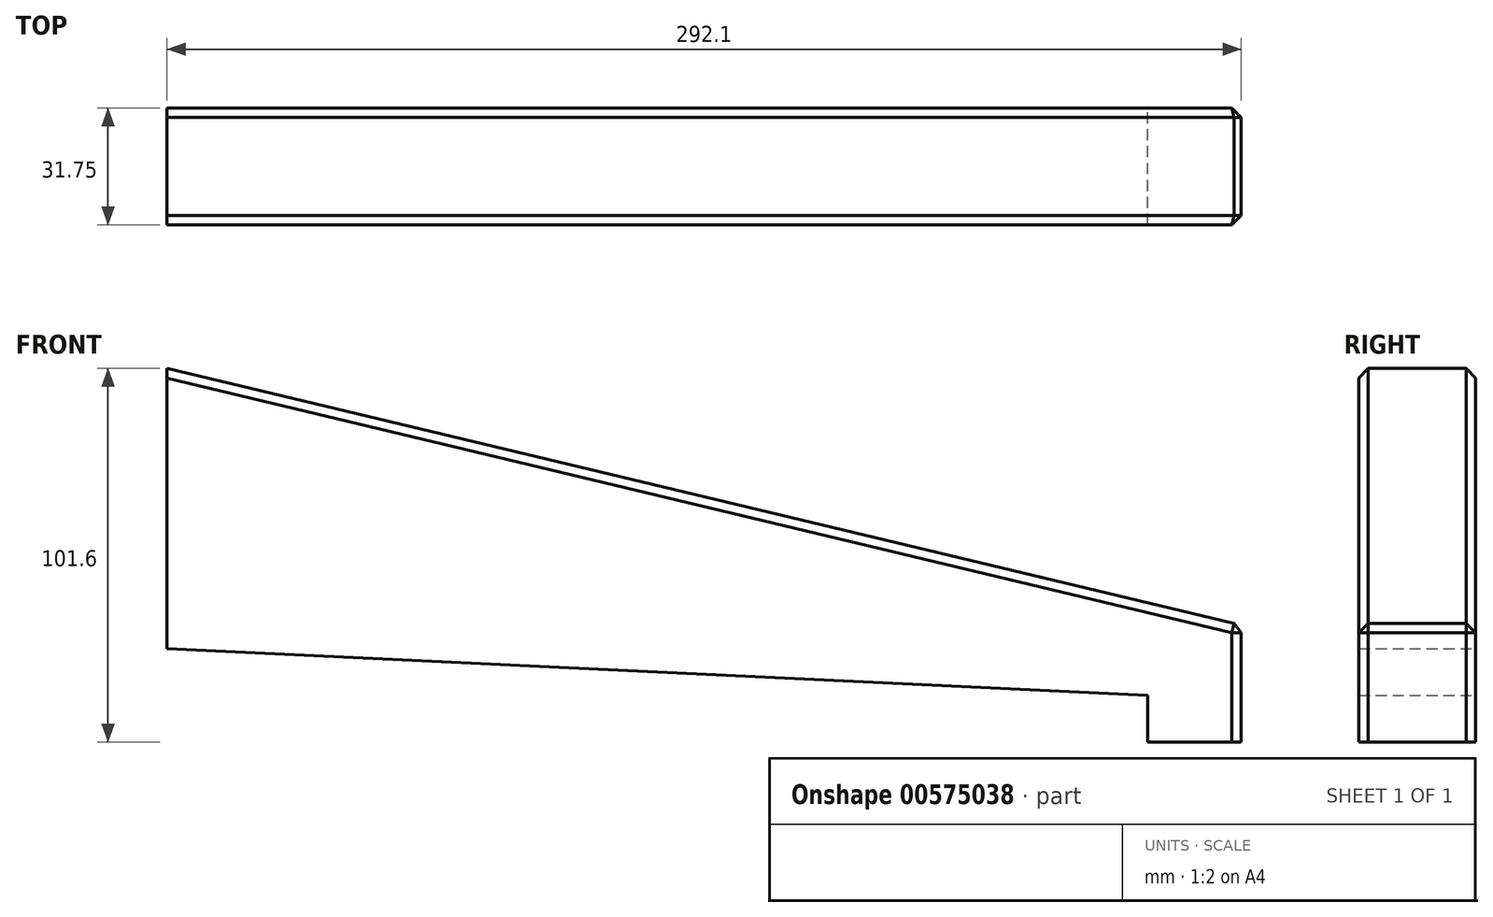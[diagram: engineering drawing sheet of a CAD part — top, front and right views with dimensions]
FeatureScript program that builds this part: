
annotation { "Feature Type Name" : "Feature", "Feature Type Description" : "" }
export const myFeature = defineFeature(function(context is Context, id is Id, definition is map)
    precondition{}
    {
        {
            var Q0;
            Q0=qCreatedBy(makeId("Front.planeOp"),FACE);
            var sketch = newSketch(context, id + "F0", { "sketchPlane" : qUnion([Q0])});
            skLineSegment(sketch, "E0.right", {"start": v(146.05, 6.35) * mm, "end": v(146.05, -12.7) * mm});
            skPoint(sketch, "E0.middle", {"position": v(0, 0) * mm});
            skLineSegment(sketch, "E1", {"start": v(146.05, -12.7) * mm, "end": v(120.65, -12.7) * mm});
            skLineSegment(sketch, "E2", {"start": v(120.65, -12.7) * mm, "end": v(120.65, 0) * mm});
            skLineSegment(sketch, "E3", {"start": v(120.65, 0) * mm, "end": v(-146.05, 12.7) * mm});
            skLineSegment(sketch, "E4", {"start": v(-146.05, 12.7) * mm, "end": v(-146.05, 88.9) * mm});
            skLineSegment(sketch, "E5", {"start": v(146.05, 6.35) * mm, "end": v(146.05, 19.05) * mm});
            skLineSegment(sketch, "E6", {"start": v(-146.05, 88.9) * mm, "end": v(146.05, 19.05) * mm});
            skLineSegment(sketch, "E7", {"start": v(120.65, 0) * mm, "end": v(-146.05, 0) * mm});
            skSolve(sketch);
        }
        {
            var Q0;
            Q0=makeQuery(id+"F0.imprint","IMPRINT",FACE,{"disambiguationData":[TD([[makeQuery(id+"F0.imprint","IMPRINT",EDGE,{"derivedFrom":sQuery(id+"F0.wireOp",EDGE,"E0.right")}),-1.0]])]});
            extrude(context, id + "F1", {"entities" : qUnion([Q0]), "depth" : 31.75 * mm, "offsetDistance" : 25.4 * mm});
        }
        {
            var Q0;
            Q0=makeQuery(id+"F1.opExtrude","CAP_EDGE",EDGE,{"disambiguationData":[OSD([sQuery(id+"F0.wireOp",EDGE,"E6")])],"isStart":false});
            var Q1;
            Q1=makeQuery(id+"F1.opExtrude","CAP_EDGE",EDGE,{"disambiguationData":[OSD([sQuery(id+"F0.wireOp",EDGE,"E6")])],"isStart":true});
            var Q2;
            Q2=makeQuery(id+"F1.opExtrude","SWEPT_EDGE",EDGE,{"disambiguationData":[OSD([sQuery(id+"F0.wireOp",EDGE,"E5"),sQuery(id+"F0.wireOp",EDGE,"E6")])]});
            var Q3;
            Q3=makeQuery(id+"F1.opExtrude","CAP_EDGE",EDGE,{"disambiguationData":[OSD([sQuery(id+"F0.wireOp",EDGE,"E0.right"),sQuery(id+"F0.wireOp",EDGE,"E5")])],"isStart":true});
            var Q4;
            Q4=makeQuery(id+"F1.opExtrude","CAP_EDGE",EDGE,{"disambiguationData":[OSD([sQuery(id+"F0.wireOp",EDGE,"E0.right"),sQuery(id+"F0.wireOp",EDGE,"E5")])],"isStart":false});
            chamfer(context, id + "F2", {"entities" : qUnion([Q0, Q1, Q2, Q3, Q4]), "width" : 2.54 * mm, "tangentPropagation" : true});
        }
    });
